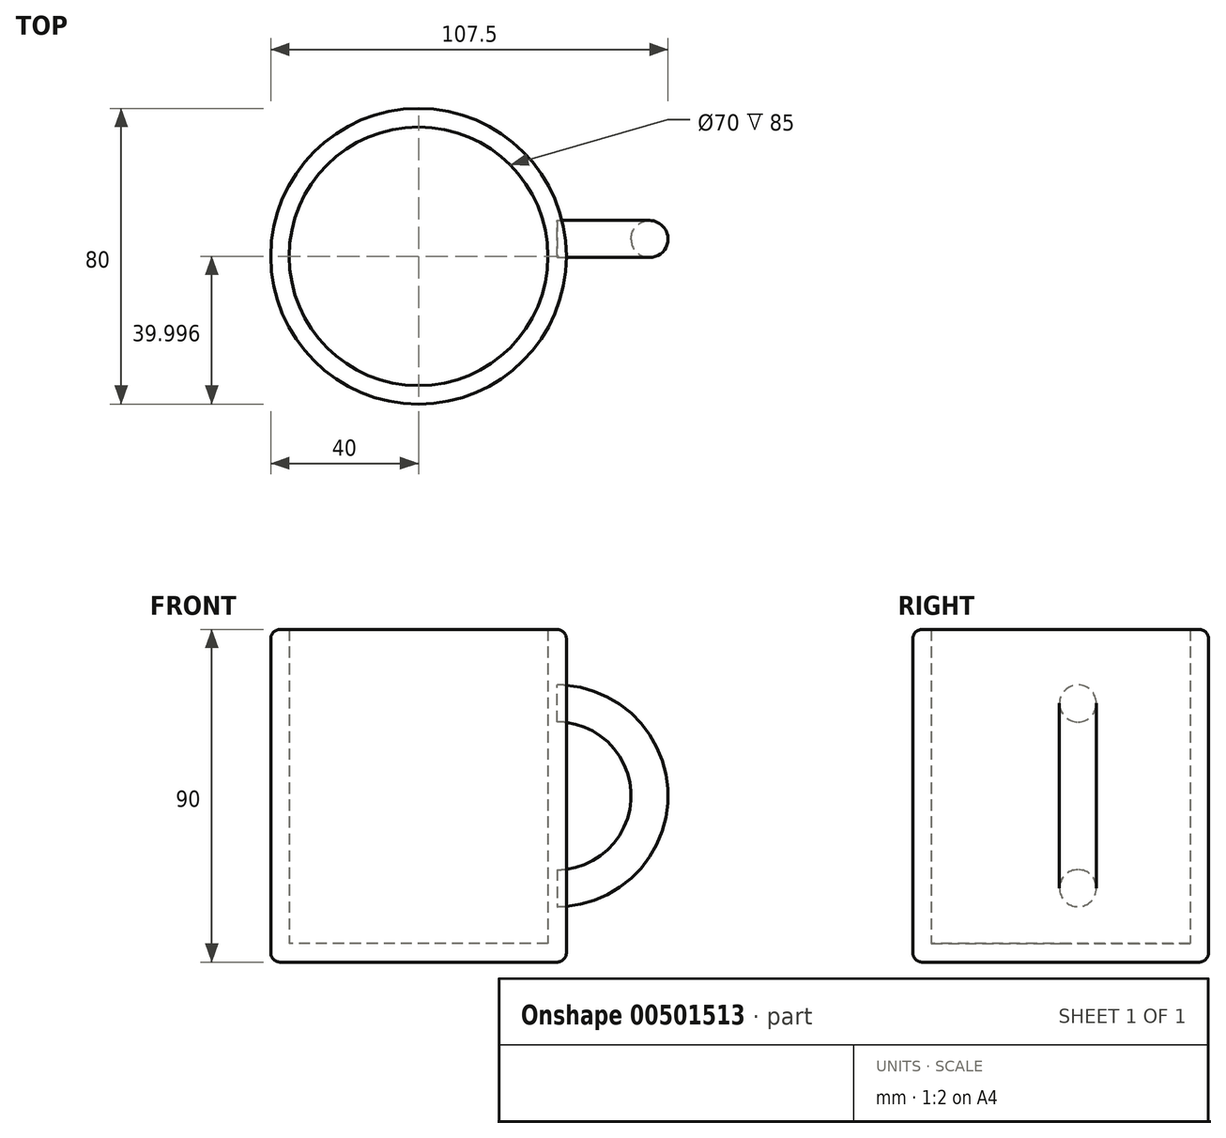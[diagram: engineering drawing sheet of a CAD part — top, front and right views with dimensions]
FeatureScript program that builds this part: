
annotation { "Feature Type Name" : "Feature", "Feature Type Description" : "" }
export const myFeature = defineFeature(function(context is Context, id is Id, definition is map)
    precondition{}
    {
        {
            var Q0;
            Q0=qCreatedBy(makeId("Top.planeOp"),FACE);
            var sketch = newSketch(context, id + "F0", { "sketchPlane" : qUnion([Q0])});
            skCircle(sketch, "E0", {"center": v(0, -4.68) * mm, "radius": 40 * mm});
            skSolve(sketch);
        }
        {
            var Q0;
            Q0 = qSketchRegion(id + "F0", true);
            extrude(context, id + "F1", {"entities" : qUnion([Q0]), "depth" : 90 * mm});
        }
        {
            var Q0;
            Q0=makeQuery(id+"F1.opExtrude","CAP_FACE",FACE,{"disambiguationData":[OSD([sQuery(id+"F0.wireOp",EDGE,"E0")])],"isStart":false});
            shell(context, id + "F2", {"entities" : qUnion([Q0]), "thickness" : 5 * mm});
        }
        {
            var Q0;
            Q0=qCreatedBy(makeId("Right.planeOp"),FACE);
            cPlane(context, id + "F3", {"entities" : qUnion([Q0]), "cplaneType" : CPlaneType.OFFSET, "offset" : 37.5 * mm, "width" : 150 * mm, "height" : 150 * mm});
        }
        {
            var Q0;
            Q0=qCreatedBy(id+"F3.planeOp",FACE);
            var sketch = newSketch(context, id + "F4", { "sketchPlane" : qUnion([Q0])});
            skCircle(sketch, "E1", {"center": v(0, 70) * mm, "radius": 5 * mm});
            skLineSegment(sketch, "E2", {"start": v(0, 45) * mm, "end": v(19.68, 45) * mm});
            skLineSegment(sketch, "E3", {"start": v(0, 70) * mm, "end": v(28.04, 70) * mm});
            skSolve(sketch);
        }
        {
            var Q0;
            Q0 = qSketchRegion(id + "F4", true);
            var Q1;
            Q1=sQuery(id+"F4.wireOp",EDGE,"E2");
            revolve(context, id + "F5", {"entities" : qUnion([Q0]), "axis" : qUnion([Q1]), "revolveType" : RevolveType.ONE_DIRECTION, "angle" : 180 * degree});
        }
        {
            var Q0;
            Q0=makeQuery(id+"F1.opExtrude","CAP_EDGE",EDGE,{"disambiguationData":[OSD([sQuery(id+"F0.wireOp",EDGE,"E0")])],"isStart":false});
            var Q1;
            Q1=makeQuery(id+"F1.opExtrude","CAP_EDGE",EDGE,{"disambiguationData":[OSD([sQuery(id+"F0.wireOp",EDGE,"E0")])],"isStart":true});
            fillet(context, id + "F6", {"entities" : qUnion([Q0, Q1]), "radius" : 2.5 * mm, "tangentPropagation" : true, "allowEdgeOverflow" : false});
        }
    });
